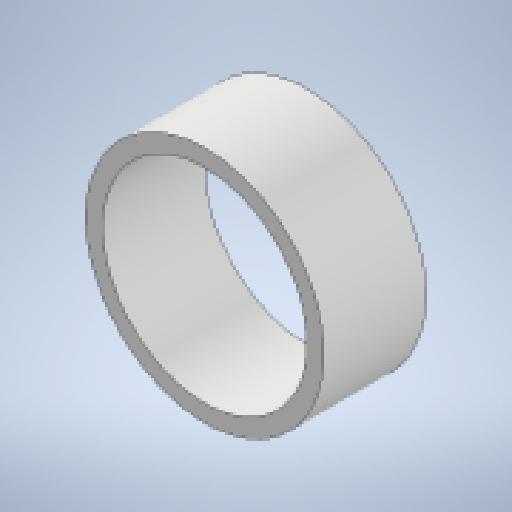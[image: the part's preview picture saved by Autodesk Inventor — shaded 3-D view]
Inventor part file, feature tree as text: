
AUTODESK INVENTOR PART (.ipt)
format: ipt  version: 2023 (Build 270158000, 158)  size: 139,264 bytes
history: native  units: in
note: dims shown in document units (in); Inventor stores cm internally (conversion verified against a paired STEP export)
features: other x3, extrude x1, sketch x1, reference x1
ambient origin geometry x8: Origin, YZ Plane, XZ Plane, XY Plane, X Axis, Y Axis, Z Axis, Center Point
bodies: Body1 (feature_tree)
feature tree (6):
  other  "Bryła1"
  extrude  "Wyciągnięcie proste1"  Depth=0.0984in
  sketch  "Szkic1"
  reference  "Odniesienie1"
  other  "Zespół2"
  other  "opona:1"
